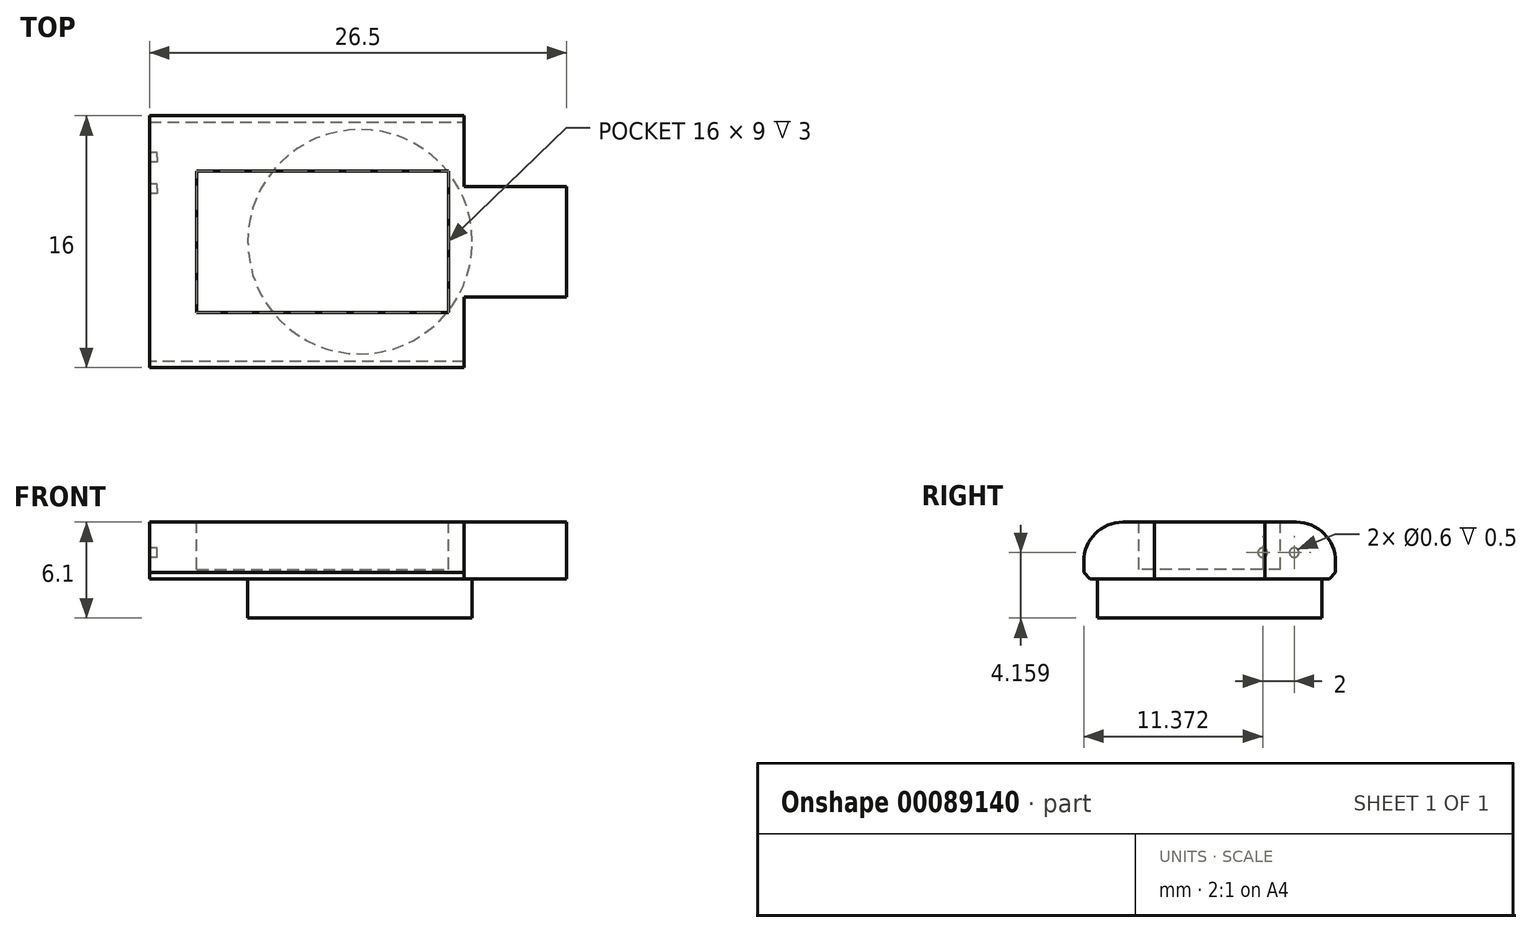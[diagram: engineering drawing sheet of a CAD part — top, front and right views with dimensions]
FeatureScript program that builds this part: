
annotation { "Feature Type Name" : "Feature", "Feature Type Description" : "" }
export const myFeature = defineFeature(function(context is Context, id is Id, definition is map)
    precondition{}
    {
        {
            var Q0;
            Q0=qCreatedBy(makeId("Top.planeOp"),FACE);
            var sketch = newSketch(context, id + "F0", { "sketchPlane" : qUnion([Q0])});
            skLineSegment(sketch, "E0.bottom", {"start": v(0, 8) * mm, "end": v(20, 8) * mm});
            skLineSegment(sketch, "E0.top", {"start": v(0, -8) * mm, "end": v(20, -8) * mm});
            skLineSegment(sketch, "E0.left", {"start": v(0, 8) * mm, "end": v(0, -8) * mm});
            skLineSegment(sketch, "E0.right", {"start": v(20, 8) * mm, "end": v(20, -8) * mm});
            skLineSegment(sketch, "E1", {"start": v(20, 3.5) * mm, "end": v(26.5, 3.5) * mm});
            skLineSegment(sketch, "E2", {"start": v(26.5, 3.5) * mm, "end": v(26.5, -3.5) * mm});
            skLineSegment(sketch, "E3", {"start": v(26.5, -3.5) * mm, "end": v(20, -3.5) * mm});
            skSolve(sketch);
        }
        {
            var Q0;
            Q0 = qSketchRegion(id + "F0", true);
            extrude(context, id + "F1", {"entities" : qUnion([Q0]), "depth" : 3.6 * mm});
        }
        {
            var Q0;
            Q0=makeQuery(id+"F1.opExtrude","CAP_FACE",FACE,{"disambiguationData":[OSD([sQuery(id+"F0.wireOp",EDGE,"E0.bottom"),sQuery(id+"F0.wireOp",EDGE,"E0.top"),sQuery(id+"F0.wireOp",EDGE,"E0.left"),sQuery(id+"F0.wireOp",EDGE,"E0.right"),sQuery(id+"F0.wireOp",EDGE,"E1"),sQuery(id+"F0.wireOp",EDGE,"E2"),sQuery(id+"F0.wireOp",EDGE,"E3")])],"isStart":true});
            var sketch = newSketch(context, id + "F2", { "sketchPlane" : qUnion([Q0])});
            skCircle(sketch, "E4", {"center": v(13.38, 0) * mm, "radius": 7.12 * mm});
            skSolve(sketch);
        }
        {
            var Q0;
            Q0=makeQuery(id+"F2.imprint","IMPRINT",FACE,{"disambiguationData":[TD([[makeQuery(id+"F2.imprint","IMPRINT",EDGE,{"derivedFrom":sQuery(id+"F2.wireOp",EDGE,"E4")}),1.0]])]});
            extrude(context, id + "F3", {"entities" : qUnion([Q0]), "operationType" : NewBodyOperationType.ADD, "depth" : 2.5 * mm});
        }
        {
            var Q0;
            Q0=makeQuery(id+"F1.opExtrude","CAP_FACE",FACE,{"disambiguationData":[OSD([sQuery(id+"F0.wireOp",EDGE,"E0.bottom"),sQuery(id+"F0.wireOp",EDGE,"E0.top"),sQuery(id+"F0.wireOp",EDGE,"E0.left"),sQuery(id+"F0.wireOp",EDGE,"E0.right"),sQuery(id+"F0.wireOp",EDGE,"E1"),sQuery(id+"F0.wireOp",EDGE,"E2"),sQuery(id+"F0.wireOp",EDGE,"E3")])],"isStart":false});
            var sketch = newSketch(context, id + "F4", { "sketchPlane" : qUnion([Q0])});
            skLineSegment(sketch, "E5.bottom", {"start": v(3, 4.5) * mm, "end": v(19, 4.5) * mm});
            skLineSegment(sketch, "E5.top", {"start": v(3, -4.5) * mm, "end": v(19, -4.5) * mm});
            skLineSegment(sketch, "E5.left", {"start": v(3, 4.5) * mm, "end": v(3, -4.5) * mm});
            skLineSegment(sketch, "E5.right", {"start": v(19, 4.5) * mm, "end": v(19, -4.5) * mm});
            skSolve(sketch);
        }
        {
            var Q0;
            Q0=makeQuery(id+"F4.imprint","IMPRINT",FACE,{"disambiguationData":[TD([[makeQuery(id+"F4.imprint","IMPRINT",EDGE,{"derivedFrom":sQuery(id+"F4.wireOp",EDGE,"E5.bottom")}),-1.0]])]});
            extrude(context, id + "F5", {"entities" : qUnion([Q0]), "operationType" : NewBodyOperationType.REMOVE, "oppositeDirection" : true, "depth" : 3 * mm});
        }
        {
            var Q0;
            Q0=makeQuery(id+"F1.opExtrude","CAP_EDGE",EDGE,{"disambiguationData":[OSD([sQuery(id+"F0.wireOp",EDGE,"E0.bottom")])],"isStart":false});
            var Q1;
            Q1=makeQuery(id+"F1.opExtrude","CAP_EDGE",EDGE,{"disambiguationData":[OSD([sQuery(id+"F0.wireOp",EDGE,"E0.top")])],"isStart":false});
            fillet(context, id + "F6", {"entities" : qUnion([Q0, Q1]), "radius" : 2.5 * mm, "tangentPropagation" : true, "allowEdgeOverflow" : false});
        }
        {
            var Q0;
            Q0=makeQuery(id+"F1.opExtrude","CAP_FACE",FACE,{"disambiguationData":[OSD([sQuery(id+"F0.wireOp",EDGE,"E0.bottom"),sQuery(id+"F0.wireOp",EDGE,"E0.top"),sQuery(id+"F0.wireOp",EDGE,"E0.left"),sQuery(id+"F0.wireOp",EDGE,"E0.right"),sQuery(id+"F0.wireOp",EDGE,"E1"),sQuery(id+"F0.wireOp",EDGE,"E2"),sQuery(id+"F0.wireOp",EDGE,"E3")])],"isStart":true});
            var sketch = newSketch(context, id + "F7", { "sketchPlane" : qUnion([Q0])});
            skLineSegment(sketch, "E6.bottom", {"start": v(0, -8) * mm, "end": v(5, -8) * mm});
            skLineSegment(sketch, "E6.top", {"start": v(0, -2.5) * mm, "end": v(5, -2.5) * mm});
            skLineSegment(sketch, "E6.left", {"start": v(0, -8) * mm, "end": v(0, -2.5) * mm});
            skLineSegment(sketch, "E6.right", {"start": v(5, -8) * mm, "end": v(5, -2.5) * mm});
            skPoint(sketch, "E7.visualSharp", {"position": v(5, -2.5) * mm});
            skSolve(sketch);
        }
        {
            var Q0;
            Q0=makeQuery(id+"F1.opExtrude","CAP_EDGE",EDGE,{"disambiguationData":[OSD([sQuery(id+"F0.wireOp",EDGE,"E0.bottom")])],"isStart":true});
            var Q1;
            Q1=makeQuery(id+"F1.opExtrude","CAP_EDGE",EDGE,{"disambiguationData":[OSD([sQuery(id+"F0.wireOp",EDGE,"E0.top")])],"isStart":true});
            chamfer(context, id + "F8", {"entities" : qUnion([Q0, Q1]), "width" : .4 * mm, "tangentPropagation" : true});
        }
        {
            var Q0;
            Q0=makeQuery(id+"F5.boolean.opBoolean","COPY",FACE,{"derivedFrom":makeQuery(id+"F5.opExtrude","CAP_FACE",FACE,{"disambiguationData":[OSD([sQuery(id+"F4.wireOp",EDGE,"E5.bottom"),sQuery(id+"F4.wireOp",EDGE,"E5.top"),sQuery(id+"F4.wireOp",EDGE,"E5.left"),sQuery(id+"F4.wireOp",EDGE,"E5.right")])],"isStart":false})});
            var Q1;
            Q1=makeQuery(id+"F5.boolean.opBoolean","COPY",FACE,{"derivedFrom":makeQuery(id+"F5.opExtrude","SWEPT_FACE",FACE,{"disambiguationData":[OSD([sQuery(id+"F4.wireOp",EDGE,"E5.bottom")])]})});
            var Q2;
            Q2=makeQuery(id+"F5.boolean.opBoolean","COPY",FACE,{"derivedFrom":makeQuery(id+"F5.opExtrude","SWEPT_FACE",FACE,{"disambiguationData":[OSD([sQuery(id+"F4.wireOp",EDGE,"E5.right")])]})});
            var Q3;
            Q3=makeQuery(id+"F5.boolean.opBoolean","COPY",FACE,{"derivedFrom":makeQuery(id+"F5.opExtrude","SWEPT_FACE",FACE,{"disambiguationData":[OSD([sQuery(id+"F4.wireOp",EDGE,"E5.left")])]})});
            var Q4;
            Q4=makeQuery(id+"F5.boolean.opBoolean","COPY",FACE,{"derivedFrom":makeQuery(id+"F5.opExtrude","SWEPT_FACE",FACE,{"disambiguationData":[OSD([sQuery(id+"F4.wireOp",EDGE,"E5.top")])]})});
            shell(context, id + "F9", {"entities" : qUnion([Q0, Q1, Q2, Q3, Q4]), "thickness" : .5 * mm});
        }
        {
            var Q0;
            Q0=makeQuery(id+"F1.opExtrude","SWEPT_FACE",FACE,{"disambiguationData":[OSD([sQuery(id+"F0.wireOp",EDGE,"E0.left")])]});
            var sketch = newSketch(context, id + "F10", { "sketchPlane" : qUnion([Q0])});
            skCircle(sketch, "E8", {"center": v(-5.37, 1.66) * mm, "radius": 0.3 * mm});
            skCircle(sketch, "E9", {"center": v(-3.37, 1.66) * mm, "radius": 0.3 * mm});
            skLineSegment(sketch, "E10", {"start": v(-5.37, 1.66) * mm, "end": v(-3.37, 1.66) * mm, "construction": true});
            skSolve(sketch);
        }
        {
            var Q0;
            Q0 = qSketchRegion(id + "F10", true);
            extrude(context, id + "F11", {"entities" : qUnion([Q0]), "operationType" : NewBodyOperationType.REMOVE, "endBound" : BoundingType.UP_TO_NEXT, "oppositeDirection" : true, "depth" : 25 * mm});
        }
        {
            var Q0;
            {var subQ0=sQuery(id+"F2.wireOp",EDGE,"E4");Q0=makeQuery(id+"F9.opShell","OFFSET_FACE",FACE,{"disambiguationData":[OSD([subQ0]),TDD([makeQuery(id+"F3.opExtrude","CAP_FACE",FACE,{"disambiguationData":[OSD([subQ0])],"isStart":false})])]});}
            var Q1;
            {var subQ0=sQuery(id+"F0.wireOp",EDGE,"E3");var subQ1=sQuery(id+"F0.wireOp",EDGE,"E2");var subQ2=sQuery(id+"F0.wireOp",EDGE,"E1");var subQ3=sQuery(id+"F0.wireOp",EDGE,"E0.right");var subQ4=sQuery(id+"F0.wireOp",EDGE,"E0.left");var subQ5=sQuery(id+"F0.wireOp",EDGE,"E0.top");var subQ6=sQuery(id+"F0.wireOp",EDGE,"E0.bottom");Q1=makeQuery(id+"F9.opShell","OFFSET_FACE",FACE,{"disambiguationData":[OSD([subQ6,subQ5,subQ4,subQ3,subQ2,subQ1,subQ0]),TDD([makeQuery(id+"F1.opExtrude","CAP_FACE",FACE,{"disambiguationData":[OSD([subQ6,subQ5,subQ4,subQ3,subQ2,subQ1,subQ0])],"isStart":true})])]});}
            extrude(context, id + "F12", {"entities" : qUnion([Q0]), "endBound" : BoundingType.UP_TO_SURFACE, "depth" : 25 * mm, "endBoundEntityFace" : qUnion([Q1]), "offsetDistance" : 25 * mm});
        }
        {
            var Q0;
            Q0=makeQuery(id+"F9.opShell","OFFSET_FACE",FACE,{"disambiguationData":[OSD([sQuery(id+"F0.wireOp",EDGE,"E2")])]});
            var Q1;
            {var subQ0=sQuery(id+"F0.wireOp",EDGE,"E0.right");Q1=makeQuery(id+"F9.opShell","OFFSET_FACE",FACE,{"disambiguationData":[OSD([subQ0]),TDD([makeQuery(id+"F1.opExtrude","SWEPT_FACE",FACE,{"disambiguationData":[OSD([subQ0]),TDD([makeQuery(id+"F0.imprint","IMPRINT",EDGE,{"disambiguationData":[TD([[makeQuery(id+"F0.imprint","INTERSECT",VERTEX,{"derivedFrom":[sQuery(id+"F0.wireOp",EDGE,"E0.bottom"),subQ0]}),-1.0]])],"derivedFrom":subQ0})])]})])]});}
            extrude(context, id + "F13", {"entities" : qUnion([Q0]), "endBound" : BoundingType.UP_TO_SURFACE, "depth" : 25 * mm, "endBoundEntityFace" : qUnion([Q1]), "offsetDistance" : 25 * mm});
        }
        {
            var Q0;
            Q0=makeQuery(id+"F9.opShell","OFFSET_FACE",FACE,{"disambiguationData":[OSD([sQuery(id+"F0.wireOp",EDGE,"E0.left")])]});
            var sketch = newSketch(context, id + "F14", { "sketchPlane" : qUnion([Q0])});
            skLineSegment(sketch, "E11", {"start": v(7.5, 0.6) * mm, "end": v(7.4, 0.5) * mm});
            skLineSegment(sketch, "E12", {"start": v(7.4, 0.5) * mm, "end": v(-7.4, 0.5) * mm});
            skLineSegment(sketch, "E13", {"start": v(-7.4, 0.5) * mm, "end": v(-7.5, 0.6) * mm});
            skLineSegment(sketch, "E14", {"start": v(-7.5, 1.1) * mm, "end": v(-7.5, 0.6) * mm});
            skArc(sketch, "E15", {"start": v(-7.5, 1.1) * mm, "mid": v(-6.91, 2.51) * mm, "end": v(-5.5, 3.1) * mm});
            skLineSegment(sketch, "E16", {"start": v(5.5, 3.1) * mm, "end": v(-5.5, 3.1) * mm});
            skArc(sketch, "E17", {"start": v(5.5, 3.1) * mm, "mid": v(6.91, 2.51) * mm, "end": v(7.5, 1.1) * mm});
            skLineSegment(sketch, "E18", {"start": v(7.5, 1.1) * mm, "end": v(7.5, 0.6) * mm});
            skSolve(sketch);
        }
        {
            var Q0;
            Q0 = qSketchRegion(id + "F14", true);
            var Q1;
            {var subQ0=sQuery(id+"F0.wireOp",EDGE,"E0.right");Q1=makeQuery(id+"F9.opShell","OFFSET_FACE",FACE,{"disambiguationData":[OSD([subQ0]),TDD([makeQuery(id+"F1.opExtrude","SWEPT_FACE",FACE,{"disambiguationData":[OSD([subQ0]),TDD([makeQuery(id+"F0.imprint","IMPRINT",EDGE,{"disambiguationData":[TD([[makeQuery(id+"F0.imprint","INTERSECT",VERTEX,{"derivedFrom":[sQuery(id+"F0.wireOp",EDGE,"E0.bottom"),subQ0]}),-1.0]])],"derivedFrom":subQ0})])]})])]});}
            extrude(context, id + "F15", {"entities" : qUnion([Q0]), "operationType" : NewBodyOperationType.ADD, "endBound" : BoundingType.UP_TO_SURFACE, "depth" : 25 * mm, "endBoundEntityFace" : qUnion([Q1]), "offsetDistance" : 25 * mm});
        }
        {
            var Q0;
            Q0=makeQuery(id+"F1.opExtrude","CAP_FACE",FACE,{"disambiguationData":[OSD([sQuery(id+"F0.wireOp",EDGE,"E0.bottom"),sQuery(id+"F0.wireOp",EDGE,"E0.top"),sQuery(id+"F0.wireOp",EDGE,"E0.left"),sQuery(id+"F0.wireOp",EDGE,"E0.right"),sQuery(id+"F0.wireOp",EDGE,"E1"),sQuery(id+"F0.wireOp",EDGE,"E2"),sQuery(id+"F0.wireOp",EDGE,"E3")])],"isStart":false});
            var sketch = newSketch(context, id + "F16", { "sketchPlane" : qUnion([Q0])});
            skLineSegment(sketch, "E19.bottom", {"start": v(3, 4.5) * mm, "end": v(19, 4.5) * mm});
            skLineSegment(sketch, "E19.top", {"start": v(3, -4.5) * mm, "end": v(19, -4.5) * mm});
            skLineSegment(sketch, "E19.left", {"start": v(3, 4.5) * mm, "end": v(3, -4.5) * mm});
            skLineSegment(sketch, "E19.right", {"start": v(19, 4.5) * mm, "end": v(19, -4.5) * mm});
            skSolve(sketch);
        }
        {
            var Q0;
            Q0 = qSketchRegion(id + "F16", true);
            extrude(context, id + "F17", {"entities" : qUnion([Q0]), "operationType" : NewBodyOperationType.REMOVE, "oppositeDirection" : true, "depth" : 3 * mm, "offsetDistance" : 25 * mm});
        }
    });
